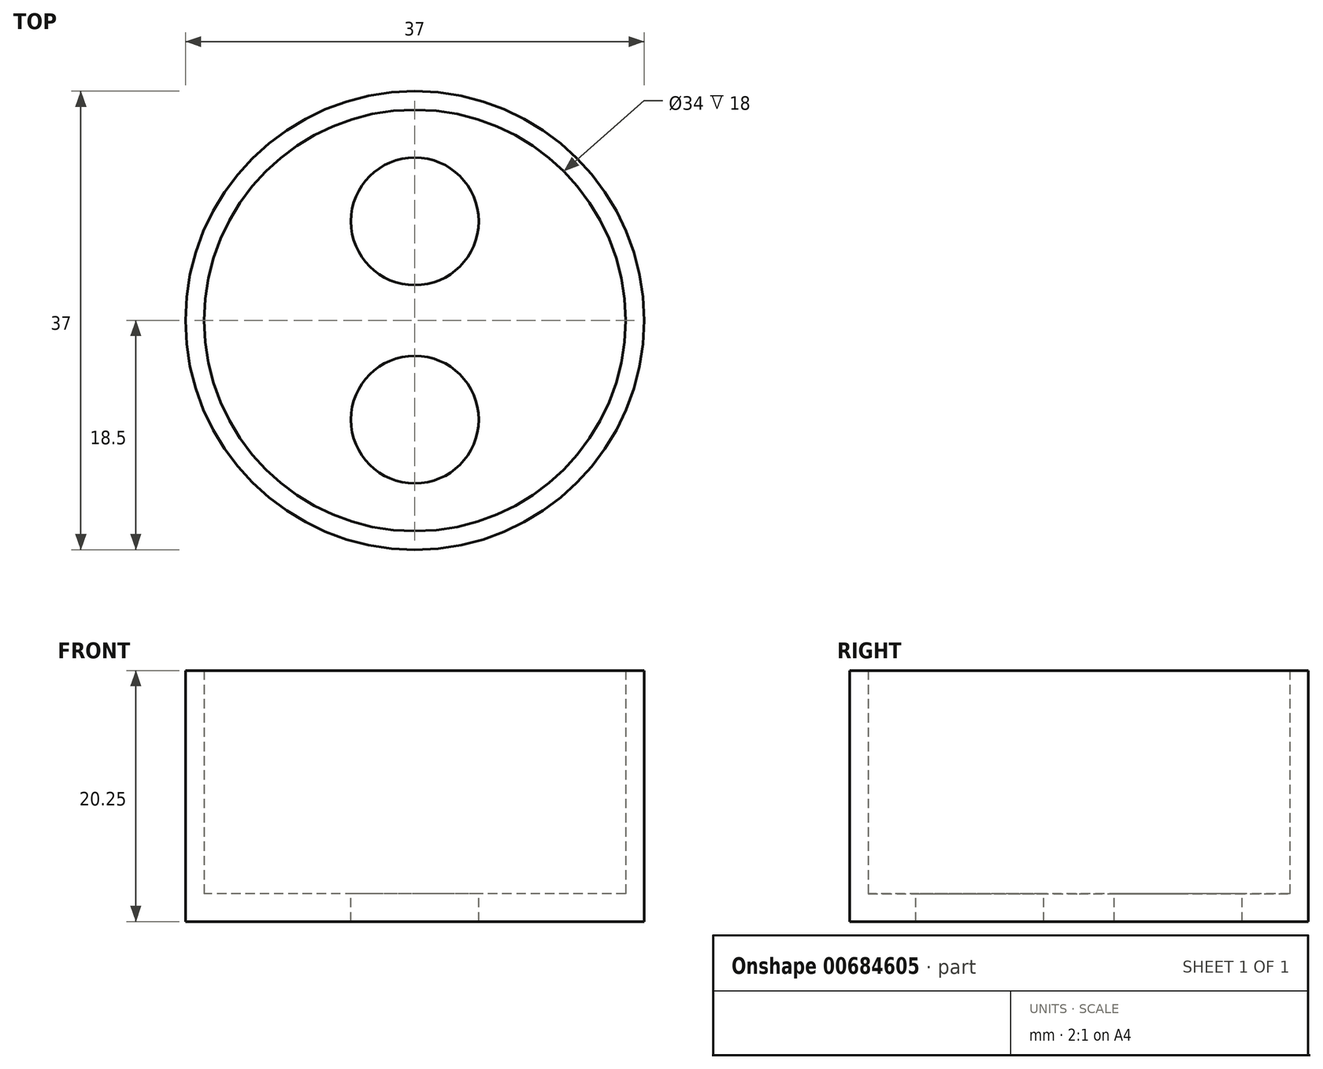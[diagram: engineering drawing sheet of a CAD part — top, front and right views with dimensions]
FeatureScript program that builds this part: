
annotation { "Feature Type Name" : "Feature", "Feature Type Description" : "" }
export const myFeature = defineFeature(function(context is Context, id is Id, definition is map)
    precondition{}
    {
        {
            assignVariable(context, id + "F0", {"name" : "btWandStaerke", "anyValue" : 1.5 * mm});
        }
        {
            var Q0;
            Q0=qCreatedBy(makeId("Top.planeOp"),FACE);
            var sketch = newSketch(context, id + "F1", { "sketchPlane" : qUnion([Q0])});
            skCircle(sketch, "E0", {"center": v(0, 0) * mm, "radius": 17 * mm});
            skCircle(sketch, "E1", {"center": v(0, 8) * mm, "radius": 5.15 * mm});
            skCircle(sketch, "E2", {"center": v(0, 0) * mm, "radius": 18.5 * mm});
            skCircle(sketch, "E3", {"center": v(0, -8) * mm, "radius": 5.15 * mm});
            skSolve(sketch);
        }
        {
            var Q0;
            Q0=makeQuery(id+"F1.imprint","IMPRINT",FACE,{"disambiguationData":[TD([[makeQuery(id+"F1.imprint","IMPRINT",EDGE,{"derivedFrom":sQuery(id+"F1.wireOp",EDGE,"E0")}),-1.0]])]});
            var Q1;
            Q1=makeQuery(id+"F1.imprint","IMPRINT",FACE,{"disambiguationData":[TD([[makeQuery(id+"F1.imprint","IMPRINT",EDGE,{"derivedFrom":sQuery(id+"F1.wireOp",EDGE,"E0")}),1.0]])]});
            extrude(context, id + "F2", {"entities" : qUnion([Q0, Q1]), "oppositeDirection" : true, "depth" : getVariable(context, 'btWandStaerke') * 1.5, "offsetDistance" : 25 * mm});
        }
        {
            var Q0;
            Q0=makeQuery(id+"F1.imprint","IMPRINT",FACE,{"disambiguationData":[TD([[makeQuery(id+"F1.imprint","IMPRINT",EDGE,{"derivedFrom":sQuery(id+"F1.wireOp",EDGE,"E0")}),-1.0]])]});
            extrude(context, id + "F3", {"entities" : qUnion([Q0]), "operationType" : NewBodyOperationType.ADD, "depth" : 18 * mm, "offsetDistance" : 25 * mm});
        }
    });
